# Revit family: Tyco_Valve_TJR_OS&Y_16inch_FxF_TJRX4000001_Native
name_source: partatom
category: Pipe Accessories
revit_build: Autodesk Revit 2016 (Build: 20150220_1215(x64)
units: mm (PartAtom-declared; Revit-internal decimal feet)

## family parameters
Always vertical = Yes
Cut with Voids When Loaded = No
OmniClass Number = 23.65.55.14.17
OmniClass Title = Adjusting/Controlling Valves for Liquid Services
Part Type = Valve - Breaks Into
Round Connector Dimension = Use Diameter
Shared = No
Work Plane-Based = No

## types (1)
- Tyco_Valve_TJR_OS&Y_16inch_FxF_TJRX4000001_Native
    COBie = Yes
    COBie.Component.Description = Gate Valves FxF DN400 (F)
    COBie.Component.Name = Valves:Gate Valve FxF
    COBie.Type = Yes
    COBie.Type.AssetType = Fixed
    COBie.Type.Category = Pr_65_54_95_97:Valves
    COBie.Type.Manufacturer = Tyco Fire Protection Products
    COBie.Type.Material = Ductile Iron
    COBie.Type.ModelNumber = TJRX4000001
    COBie.Type.ModelReference = Gate Valves FxF DN400 (F)
    COBie.Type.NominalHeight = 0' - 0"
    COBie.Type.NominalLength = 0' - 0"
    COBie.Type.NominalWidth = 0' - 0"
    COBie.Type.ReplacementCost = 0 $
    COBie.Type.Size = 16"(DN400) x 16"(DN400)
    COBie.Type.WarrantyGuarantorParts = http://tycofsbp.com
TFPPTerms_of_Sale.pdf
    Description = Model TJR Resilient seated Gate valve OS&Y 16" (DN400) with FxF DIN_TJRX4000001
    Finish_ = Tyco - Epoxy coating
    Flange Diameter 1 = 23"
    Flange Diameter 2 = 23"
    Length X = 16"
    Length Y = 54"
    Manufacturer = Tyco Fire Protection Products
    Manufacturer URL = www.tyco-fire.com
    Material_ = Ductile Iron
    Model = OS&Y Gate FxF - Resilient seated
    Nominal Diameter 1 = 16"
    Nominal Diameter 2 = 16"
    Outside Diameter 1 = 16"
    Outside Diameter 2 = 16"
    Part No = TJRX4000001
    Style Id = 0
    Takeout 1 = 0"
    Takeout 2 = 0"
    Technical Data Sheet No = TFP1541

## geometry (parser evidence)
native form markers: Blend x2, Sweep x59
no freeform markers — native parametric forms only
